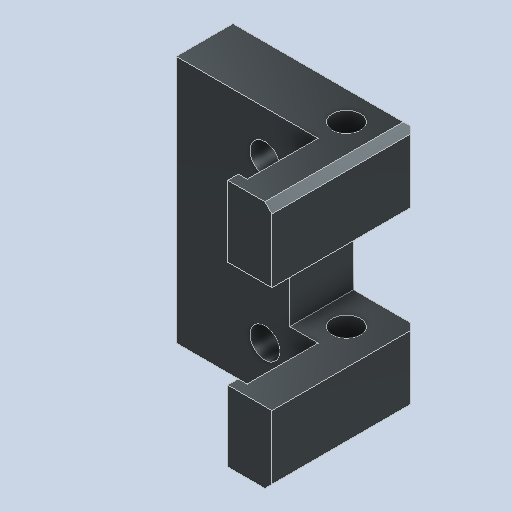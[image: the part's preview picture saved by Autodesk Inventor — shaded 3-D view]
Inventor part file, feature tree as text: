
AUTODESK INVENTOR PART (.ipt)
format: ipt  version: 2023.2 (Build 272271030, 271C)  size: 322,048 bytes
history: native  units: mm
features: chamfer x7, sketch x5, extrude x2, plane x2, mirror x2, hole x2
ambient origin geometry x8: Origin, YZ Plane, XZ Plane, XY Plane, X Axis, Y Axis, Z Axis, Center Point
bodies: Solid1 (feature_tree)
feature tree (20):
  extrude  "Extrusion1"  Depth=18.0mm
  sketch  "Sketch2"  dims[d4=12.5mm d5=10.0mm]
  extrude  "Extrusion2"  Depth=10.0mm
  plane  "Work Plane1"
  mirror  "Mirror1"
  plane  "Work Plane2"
  mirror  "Mirror2"
  hole  "Hole1"  [1 undecoded]
  hole  "Hole2"  [1 undecoded]
  chamfer  "Chamfer1"  Distance=20.0mm
  chamfer  "Chamfer2"  Distance=18.0mm
  chamfer  "Chamfer3"  Distance=15.0mm
  chamfer  "Chamfer4"  Distance=15.0mm
  chamfer  "Chamfer5"  [1 undecoded]
  chamfer  "Chamfer6"  Distance=15.0mm
  chamfer  "Chamfer7"  Distance=15.0mm
  sketch  "Sketch1"  dims[d1=40.0mm d2=18.0mm]
  sketch  "Sketch3"  dims[d6=3.0mm d7=20.0mm]
  sketch  "Sketch4"  dims[d8=8.0mm d9=10.0mm]
  sketch  "Sketch5"  dims[d10=10.0mm d11=20.0mm d12=0.0mm d13=18.0mm d14=15.0mm d15=0.0mm d16=15.0mm d17=0.0mm d18=15.0mm d19=15.0mm d20=25.0mm d21=12.5mm d22=12.5mm d23=25.0mm d24=15.0mm d25=6.0mm d26=4.0mm d27=2.0mm d28=90.0deg d29=8.0mm d30=20.594885mm d31=8.4mm d32=8.4mm d33=25.0mm d34=12.5mm d35=25.0mm d36=12.5mm d37=8.4mm d38=6.0mm d39=4.0mm d40=2.0mm d41=90.0deg d42=8.0mm d43=20.594885mm d44=2.0mm d45=2.0mm d46=45.0deg d47=2.0mm d48=2.0mm d49=45.0deg d50=2.0mm d51=2.0mm d52=45.0deg d53=2.0mm d54=2.0mm d55=45.0deg d56=2.0mm d57=2.0mm d58=45.0deg d59=2.0mm d60=2.0mm d61=45.0deg d62=2.0mm d63=2.0mm d64=45.0deg]
note: 3 required parameter values undecoded (feature->parameter linkage not recoverable at this tier; creation-order binding heuristic only, values carry confidence <= 0.55)
